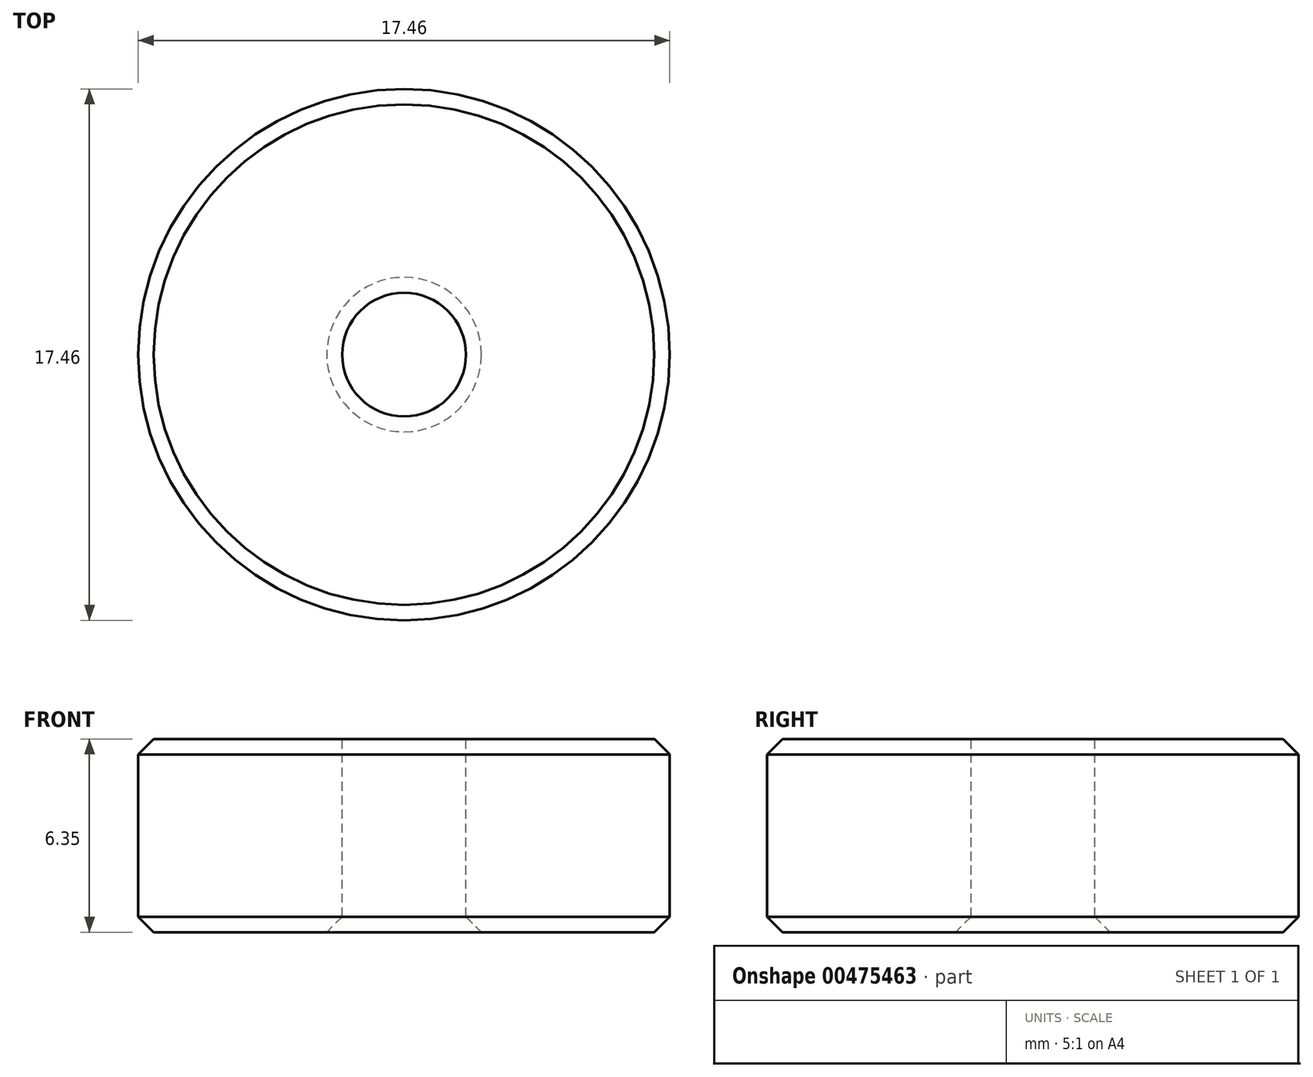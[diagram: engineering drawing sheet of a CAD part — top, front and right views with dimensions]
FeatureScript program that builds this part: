
annotation { "Feature Type Name" : "Feature", "Feature Type Description" : "" }
export const myFeature = defineFeature(function(context is Context, id is Id, definition is map)
    precondition{}
    {
        {
            var Q0;
            Q0=qCreatedBy(makeId("Top.planeOp"),FACE);
            var sketch = newSketch(context, id + "F0", { "sketchPlane" : qUnion([Q0])});
            skCircle(sketch, "E0", {"center": v(0, 0) * mm, "radius": 8.73 * mm});
            skSolve(sketch);
        }
        {
            var Q0;
            Q0 = qSketchRegion(id + "F0", true);
            extrude(context, id + "F1", {"entities" : qUnion([Q0]), "depth" : 6.35 * mm});
        }
        {
            var Q0;
            Q0=makeQuery(id+"F1.opExtrude","CAP_FACE",FACE,{"disambiguationData":[OSD([sQuery(id+"F0.wireOp",EDGE,"E0")])],"isStart":false});
            var sketch = newSketch(context, id + "F2", { "sketchPlane" : qUnion([Q0])});
            skCircle(sketch, "E1", {"center": v(0, 0) * mm, "radius": 2.03 * mm});
            skSolve(sketch);
        }
        {
            var Q0;
            Q0 = qSketchRegion(id + "F2", true);
            extrude(context, id + "F3", {"entities" : qUnion([Q0]), "operationType" : NewBodyOperationType.REMOVE, "oppositeDirection" : true, "depth" : 25.4 * mm});
        }
        {
            var Q0;
            Q0=makeQuery(id+"F1.opExtrude","CAP_EDGE",EDGE,{"disambiguationData":[OSD([sQuery(id+"F0.wireOp",EDGE,"E0")])],"isStart":true});
            var Q1;
            Q1=makeQuery(id+"F1.opExtrude","CAP_EDGE",EDGE,{"disambiguationData":[OSD([sQuery(id+"F0.wireOp",EDGE,"E0")])],"isStart":false});
            var Q2;
            Q2=makeQuery(id+"F3.boolean.opBoolean","COPY",EDGE,{"derivedFrom":makeQuery(id+"F3.opExtrude","CAP_EDGE",EDGE,{"disambiguationData":[OSD([sQuery(id+"F2.wireOp",EDGE,"E1")])],"isStart":true})});
            var Q3;
            Q3=makeQuery(id+"F3.boolean.opBoolean","INTERSECT",EDGE,{"derivedFrom":[makeQuery(id+"F1.opExtrude","CAP_FACE",FACE,{"disambiguationData":[OSD([sQuery(id+"F0.wireOp",EDGE,"E0")])],"isStart":true}),makeQuery(id+"F3.opExtrude","SWEPT_FACE",FACE,{"disambiguationData":[OSD([sQuery(id+"F2.wireOp",EDGE,"E1")])]})]});
            chamfer(context, id + "F4", {"entities" : qUnion([Q0, Q1, Q2, Q3]), "width" : 0.5 * mm, "tangentPropagation" : true});
        }
    });
